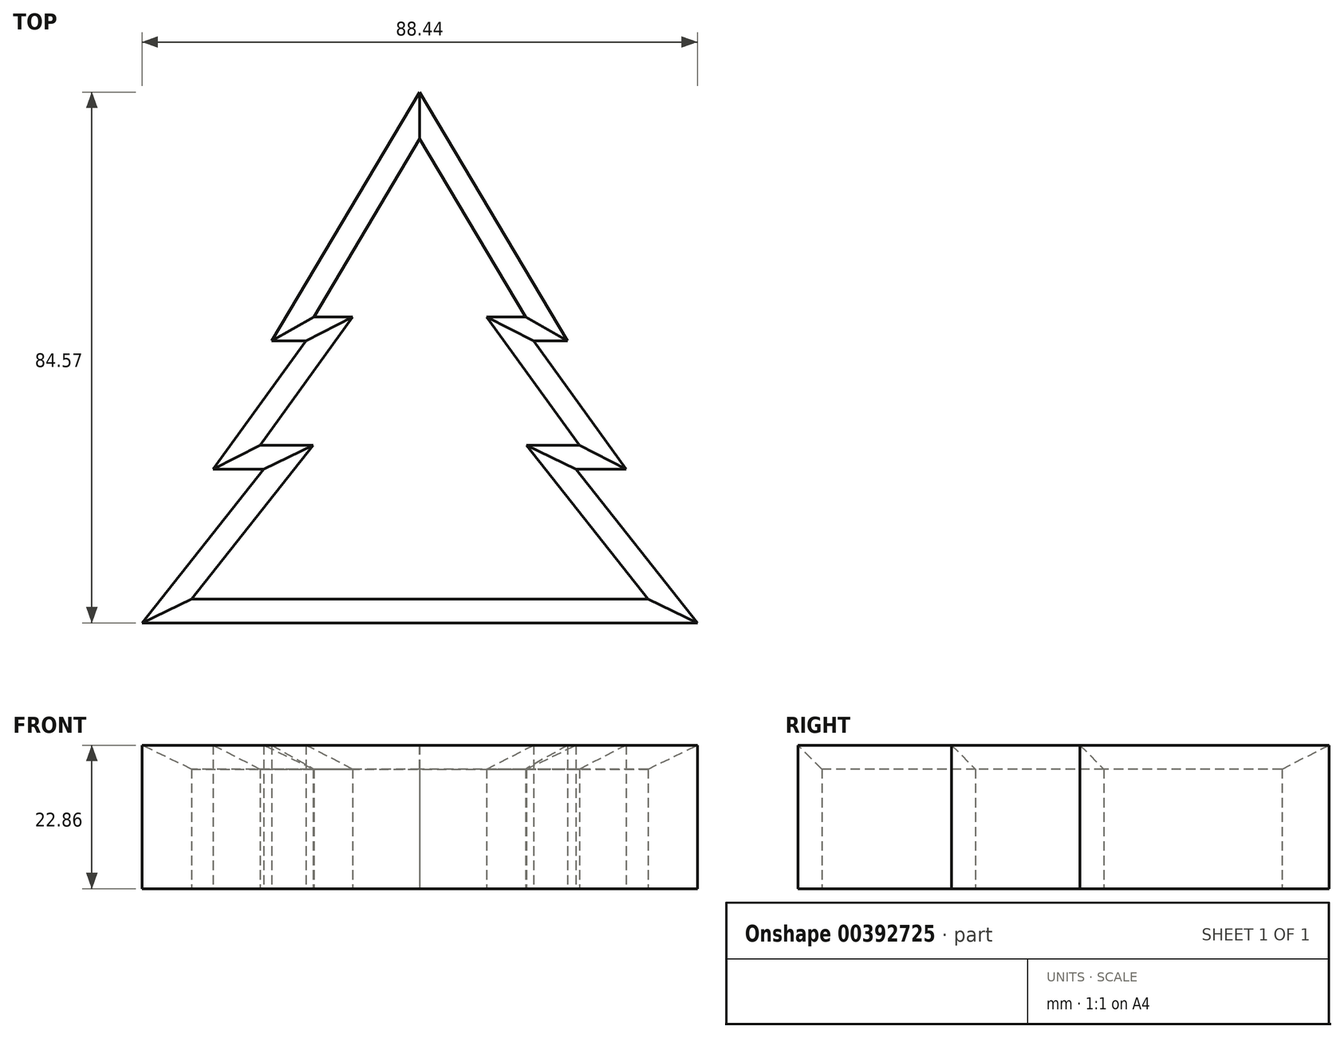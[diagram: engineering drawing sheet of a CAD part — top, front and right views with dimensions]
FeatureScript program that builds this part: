
annotation { "Feature Type Name" : "Feature", "Feature Type Description" : "" }
export const myFeature = defineFeature(function(context is Context, id is Id, definition is map)
    precondition{}
    {
        {
            var Q0;
            Q0=qCreatedBy(makeId("Top.planeOp"),FACE);
            var sketch = newSketch(context, id + "F0", { "sketchPlane" : qUnion([Q0])});
            skLineSegment(sketch, "E0", {"start": v(0, 0) * mm, "end": v(0, 4.38) * mm});
            skLineSegment(sketch, "E1", {"start": v(0, 77.68) * mm, "end": v(16.86, 49.3) * mm});
            skLineSegment(sketch, "E2", {"start": v(16.86, 49.3) * mm, "end": v(10.67, 49.3) * mm});
            skLineSegment(sketch, "E3", {"start": v(10.67, 49.3) * mm, "end": v(25.44, 28.86) * mm});
            skLineSegment(sketch, "E4", {"start": v(25.44, 28.86) * mm, "end": v(17, 28.86) * mm});
            skLineSegment(sketch, "E5", {"start": v(17, 28.86) * mm, "end": v(36.35, 4.38) * mm});
            skLineSegment(sketch, "E6", {"start": v(36.35, 4.38) * mm, "end": v(0, 4.38) * mm});
            skLineSegment(sketch, "E7.MirrorCS", {"start": v(-17, 28.86) * mm, "end": v(-36.35, 4.38) * mm});
            skLineSegment(sketch, "E8.MirrorCS", {"start": v(0, 77.68) * mm, "end": v(-16.86, 49.3) * mm});
            skLineSegment(sketch, "E9.MirrorCS", {"start": v(-36.35, 4.38) * mm, "end": v(0, 4.38) * mm});
            skLineSegment(sketch, "E10.MirrorCS", {"start": v(-25.44, 28.86) * mm, "end": v(-17, 28.86) * mm});
            skLineSegment(sketch, "E11.MirrorCS", {"start": v(-10.67, 49.3) * mm, "end": v(-25.44, 28.86) * mm});
            skLineSegment(sketch, "E12.MirrorCS", {"start": v(-16.86, 49.3) * mm, "end": v(-10.67, 49.3) * mm});
            skLineSegment(sketch, "E13.0", {"start": v(-24.87, 25.05) * mm, "end": v(-44.22, 0.57) * mm});
            skLineSegment(sketch, "E13.1", {"start": v(18.13, 45.48) * mm, "end": v(32.9, 25.05) * mm});
            skLineSegment(sketch, "E13.2", {"start": v(32.9, 25.05) * mm, "end": v(24.87, 25.05) * mm});
            skLineSegment(sketch, "E13.3", {"start": v(24.87, 25.05) * mm, "end": v(44.22, 0.57) * mm});
            skLineSegment(sketch, "E13.4", {"start": v(44.22, 0.57) * mm, "end": v(0, 0.57) * mm});
            skLineSegment(sketch, "E13.5", {"start": v(23.55, 45.48) * mm, "end": v(18.13, 45.48) * mm});
            skLineSegment(sketch, "E13.6", {"start": v(-44.22, 0.57) * mm, "end": v(0, 0.57) * mm});
            skLineSegment(sketch, "E13.7", {"start": v(0, 85.14) * mm, "end": v(23.55, 45.48) * mm});
            skLineSegment(sketch, "E13.8", {"start": v(0, 85.14) * mm, "end": v(-23.55, 45.48) * mm});
            skLineSegment(sketch, "E13.9", {"start": v(-23.55, 45.48) * mm, "end": v(-18.13, 45.48) * mm});
            skLineSegment(sketch, "E13.10", {"start": v(-18.13, 45.48) * mm, "end": v(-32.9, 25.05) * mm});
            skLineSegment(sketch, "E13.11", {"start": v(-32.9, 25.05) * mm, "end": v(-24.87, 25.05) * mm});
            skSolve(sketch);
        }
        {
            var Q0;
            Q0=makeQuery(id+"F0.imprint","IMPRINT",FACE,{"disambiguationData":[TD([[makeQuery(id+"F0.imprint","IMPRINT",EDGE,{"derivedFrom":sQuery(id+"F0.wireOp",EDGE,"E1")}),1.0]])]});
            extrude(context, id + "F1", {"entities" : qUnion([Q0]), "depth" : 25.4 * mm});
        }
        {
            var Q0;
            Q0=makeQuery(id+"F1.opExtrude","CAP_EDGE",EDGE,{"disambiguationData":[OSD([sQuery(id+"F0.wireOp",EDGE,"E3")])],"isStart":false});
            var Q1;
            Q1=makeQuery(id+"F1.opExtrude","CAP_EDGE",EDGE,{"disambiguationData":[OSD([sQuery(id+"F0.wireOp",EDGE,"E4")])],"isStart":false});
            var Q2;
            Q2=makeQuery(id+"F1.opExtrude","CAP_EDGE",EDGE,{"disambiguationData":[OSD([sQuery(id+"F0.wireOp",EDGE,"E5")])],"isStart":false});
            var Q3;
            Q3=makeQuery(id+"F1.opExtrude","CAP_EDGE",EDGE,{"disambiguationData":[OSD([sQuery(id+"F0.wireOp",EDGE,"E6"),sQuery(id+"F0.wireOp",EDGE,"E9.MirrorCS")])],"isStart":false});
            var Q4;
            Q4=makeQuery(id+"F1.opExtrude","CAP_EDGE",EDGE,{"disambiguationData":[OSD([sQuery(id+"F0.wireOp",EDGE,"E7.MirrorCS")])],"isStart":false});
            var Q5;
            Q5=makeQuery(id+"F1.opExtrude","CAP_EDGE",EDGE,{"disambiguationData":[OSD([sQuery(id+"F0.wireOp",EDGE,"E10.MirrorCS")])],"isStart":false});
            var Q6;
            Q6=makeQuery(id+"F1.opExtrude","CAP_EDGE",EDGE,{"disambiguationData":[OSD([sQuery(id+"F0.wireOp",EDGE,"E11.MirrorCS")])],"isStart":false});
            var Q7;
            Q7=makeQuery(id+"F1.opExtrude","CAP_EDGE",EDGE,{"disambiguationData":[OSD([sQuery(id+"F0.wireOp",EDGE,"E12.MirrorCS")])],"isStart":false});
            var Q8;
            Q8=makeQuery(id+"F1.opExtrude","CAP_EDGE",EDGE,{"disambiguationData":[OSD([sQuery(id+"F0.wireOp",EDGE,"E8.MirrorCS")])],"isStart":false});
            var Q9;
            Q9=makeQuery(id+"F1.opExtrude","CAP_EDGE",EDGE,{"disambiguationData":[OSD([sQuery(id+"F0.wireOp",EDGE,"E1")])],"isStart":false});
            var Q10;
            Q10=makeQuery(id+"F1.opExtrude","CAP_EDGE",EDGE,{"disambiguationData":[OSD([sQuery(id+"F0.wireOp",EDGE,"E2")])],"isStart":false});
            chamfer(context, id + "F2", {"entities" : qUnion([Q0, Q1, Q2, Q3, Q4, Q5, Q6, Q7, Q8, Q9, Q10]), "width" : 6.35 * mm, "tangentPropagation" : true});
        }
    });
